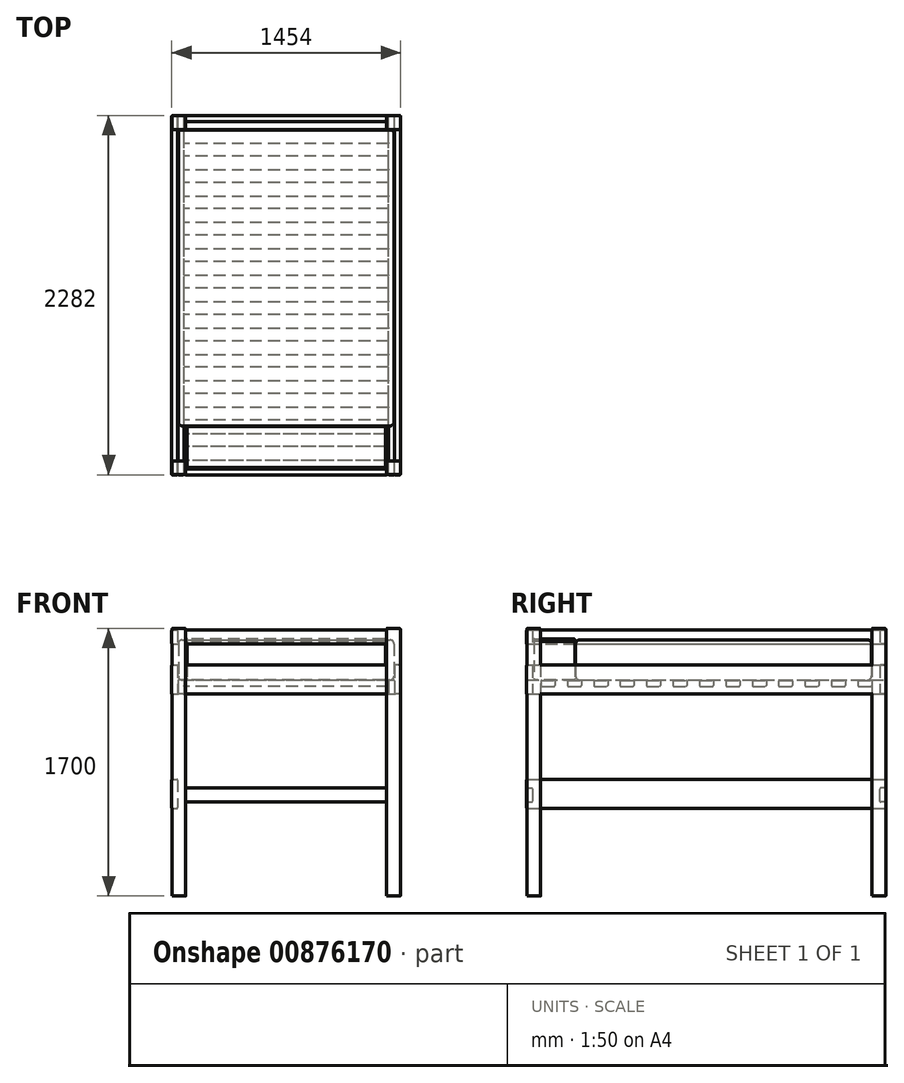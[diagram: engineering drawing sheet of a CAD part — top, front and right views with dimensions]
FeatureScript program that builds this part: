
annotation { "Feature Type Name" : "Feature", "Feature Type Description" : "" }
export const myFeature = defineFeature(function(context is Context, id is Id, definition is map)
    precondition{}
    {
        {
            var Q0;
            Q0=qCreatedBy(makeId("Top.planeOp"),FACE);
            var sketch = newSketch(context, id + "F0", { "sketchPlane" : qUnion([Q0])});
            skLineSegment(sketch, "E0.bottom", {"start": v(-720, -1052.5) * mm, "end": v(-642.5, -1052.5) * mm});
            skLineSegment(sketch, "E0.top", {"start": v(-720, -1140) * mm, "end": v(-642.5, -1140) * mm});
            skLineSegment(sketch, "E0.left", {"start": v(-725, -1057.5) * mm, "end": v(-725, -1135) * mm});
            skLineSegment(sketch, "E0.right", {"start": v(-637.5, -1057.5) * mm, "end": v(-637.5, -1135) * mm});
            skLineSegment(sketch, "E1.bottom", {"start": v(-720, 1140) * mm, "end": v(-642.5, 1140) * mm});
            skLineSegment(sketch, "E1.top", {"start": v(-720, 1052.5) * mm, "end": v(-642.5, 1052.5) * mm});
            skLineSegment(sketch, "E1.left", {"start": v(-725, 1135) * mm, "end": v(-725, 1057.5) * mm});
            skLineSegment(sketch, "E1.right", {"start": v(-637.5, 1135) * mm, "end": v(-637.5, 1057.5) * mm});
            skLineSegment(sketch, "E2.bottom", {"start": v(642.5, 1140) * mm, "end": v(720, 1140) * mm});
            skLineSegment(sketch, "E2.top", {"start": v(642.5, 1052.5) * mm, "end": v(720, 1052.5) * mm});
            skLineSegment(sketch, "E2.left", {"start": v(637.5, 1135) * mm, "end": v(637.5, 1057.5) * mm});
            skLineSegment(sketch, "E2.right", {"start": v(725, 1135) * mm, "end": v(725, 1057.5) * mm});
            skLineSegment(sketch, "E3.bottom", {"start": v(642.5, -1052.5) * mm, "end": v(720, -1052.5) * mm});
            skLineSegment(sketch, "E3.top", {"start": v(642.5, -1140) * mm, "end": v(720, -1140) * mm});
            skLineSegment(sketch, "E3.left", {"start": v(637.5, -1057.5) * mm, "end": v(637.5, -1135) * mm});
            skLineSegment(sketch, "E3.right", {"start": v(725, -1057.5) * mm, "end": v(725, -1135) * mm});
            skPoint(sketch, "E4.visualSharp", {"position": v(-637.5, 1052.5) * mm});
            skArc(sketch, "E4.filletArc", {"start": v(-642.5, 1052.5) * mm, "mid": v(-638.96, 1053.96) * mm, "end": v(-637.5, 1057.5) * mm});
            skPoint(sketch, "E5.visualSharp", {"position": v(-725, 1140) * mm});
            skArc(sketch, "E5.filletArc", {"start": v(-720, 1140) * mm, "mid": v(-723.54, 1138.54) * mm, "end": v(-725, 1135) * mm});
            skPoint(sketch, "E6.visualSharp", {"position": v(-725, 1052.5) * mm});
            skArc(sketch, "E6.filletArc", {"start": v(-725, 1057.5) * mm, "mid": v(-723.54, 1053.96) * mm, "end": v(-720, 1052.5) * mm});
            skPoint(sketch, "E7.visualSharp", {"position": v(-637.5, 1140) * mm});
            skArc(sketch, "E7.filletArc", {"start": v(-637.5, 1135) * mm, "mid": v(-638.96, 1138.54) * mm, "end": v(-642.5, 1140) * mm});
            skPoint(sketch, "E8.visualSharp", {"position": v(637.5, 1052.5) * mm});
            skArc(sketch, "E8.filletArc", {"start": v(637.5, 1057.5) * mm, "mid": v(638.96, 1053.96) * mm, "end": v(642.5, 1052.5) * mm});
            skPoint(sketch, "E9.visualSharp", {"position": v(725, 1140) * mm});
            skArc(sketch, "E9.filletArc", {"start": v(725, 1135) * mm, "mid": v(723.54, 1138.54) * mm, "end": v(720, 1140) * mm});
            skPoint(sketch, "E10.visualSharp", {"position": v(725, 1052.5) * mm});
            skArc(sketch, "E10.filletArc", {"start": v(720, 1052.5) * mm, "mid": v(723.54, 1053.96) * mm, "end": v(725, 1057.5) * mm});
            skPoint(sketch, "E11.visualSharp", {"position": v(637.5, 1140) * mm});
            skArc(sketch, "E11.filletArc", {"start": v(642.5, 1140) * mm, "mid": v(638.96, 1138.54) * mm, "end": v(637.5, 1135) * mm});
            skPoint(sketch, "E12.visualSharp", {"position": v(-637.5, -1140) * mm});
            skArc(sketch, "E12.filletArc", {"start": v(-642.5, -1140) * mm, "mid": v(-638.96, -1138.54) * mm, "end": v(-637.5, -1135) * mm});
            skPoint(sketch, "E13.visualSharp", {"position": v(-725, -1052.5) * mm});
            skArc(sketch, "E13.filletArc", {"start": v(-720, -1052.5) * mm, "mid": v(-723.54, -1053.96) * mm, "end": v(-725, -1057.5) * mm});
            skPoint(sketch, "E14.visualSharp", {"position": v(-725, -1140) * mm});
            skArc(sketch, "E14.filletArc", {"start": v(-725, -1135) * mm, "mid": v(-723.54, -1138.54) * mm, "end": v(-720, -1140) * mm});
            skPoint(sketch, "E15.visualSharp", {"position": v(-637.5, -1052.5) * mm});
            skArc(sketch, "E15.filletArc", {"start": v(-637.5, -1057.5) * mm, "mid": v(-638.96, -1053.96) * mm, "end": v(-642.5, -1052.5) * mm});
            skPoint(sketch, "E16.visualSharp", {"position": v(725, -1140) * mm});
            skArc(sketch, "E16.filletArc", {"start": v(720, -1140) * mm, "mid": v(723.54, -1138.54) * mm, "end": v(725, -1135) * mm});
            skPoint(sketch, "E17.visualSharp", {"position": v(637.5, -1052.5) * mm});
            skArc(sketch, "E17.filletArc", {"start": v(642.5, -1052.5) * mm, "mid": v(638.96, -1053.96) * mm, "end": v(637.5, -1057.5) * mm});
            skPoint(sketch, "E18.visualSharp", {"position": v(637.5, -1140) * mm});
            skArc(sketch, "E18.filletArc", {"start": v(637.5, -1135) * mm, "mid": v(638.96, -1138.54) * mm, "end": v(642.5, -1140) * mm});
            skPoint(sketch, "E19.visualSharp", {"position": v(725, -1052.5) * mm});
            skArc(sketch, "E19.filletArc", {"start": v(725, -1057.5) * mm, "mid": v(723.54, -1053.96) * mm, "end": v(720, -1052.5) * mm});
            skSolve(sketch);
        }
        {
            var Q0;
            Q0 = qSketchRegion(id + "F0", true);
            extrude(context, id + "F1", {"entities" : qUnion([Q0]), "depth" : 1700 * mm, "offsetDistance" : 25 * mm});
        }
        {
            var Q0;
            Q0=qCreatedBy(makeId("Front.planeOp"),FACE);
            var sketch = newSketch(context, id + "F2", { "sketchPlane" : qUnion([Q0])});
            skLineSegment(sketch, "E20.bottom", {"start": v(-722, 1466) * mm, "end": v(-694, 1466) * mm});
            skLineSegment(sketch, "E20.top", {"start": v(-722, 1282) * mm, "end": v(-694, 1282) * mm});
            skLineSegment(sketch, "E20.left", {"start": v(-727, 1461) * mm, "end": v(-727, 1287) * mm});
            skLineSegment(sketch, "E20.right", {"start": v(-689, 1461) * mm, "end": v(-689, 1287) * mm});
            skLineSegment(sketch, "E21.bottom", {"start": v(722, 1466) * mm, "end": v(694, 1466) * mm});
            skLineSegment(sketch, "E21.top", {"start": v(722, 1282) * mm, "end": v(694, 1282) * mm});
            skLineSegment(sketch, "E21.left", {"start": v(727, 1461) * mm, "end": v(727, 1287) * mm});
            skLineSegment(sketch, "E21.right", {"start": v(689, 1461) * mm, "end": v(689, 1287) * mm});
            skLineSegment(sketch, "E22.bottom", {"start": v(-722, 740) * mm, "end": v(-694, 740) * mm});
            skLineSegment(sketch, "E22.top", {"start": v(-722, 556) * mm, "end": v(-694, 556) * mm});
            skLineSegment(sketch, "E22.left", {"start": v(-727, 735) * mm, "end": v(-727, 561) * mm});
            skLineSegment(sketch, "E22.right", {"start": v(-689, 735) * mm, "end": v(-689, 561) * mm});
            skLineSegment(sketch, "E23.bottom", {"start": v(-655, 1371) * mm, "end": v(-683, 1371) * mm});
            skLineSegment(sketch, "E23.top", {"start": v(-655, 1282) * mm, "end": v(-683, 1282) * mm});
            skLineSegment(sketch, "E23.left", {"start": v(-650, 1366) * mm, "end": v(-650, 1287) * mm});
            skLineSegment(sketch, "E23.right", {"start": v(-688, 1366) * mm, "end": v(-688, 1287) * mm});
            skLineSegment(sketch, "E24.bottom", {"start": v(655, 1371) * mm, "end": v(683, 1371) * mm});
            skLineSegment(sketch, "E24.top", {"start": v(655, 1282) * mm, "end": v(683, 1282) * mm});
            skLineSegment(sketch, "E24.left", {"start": v(650, 1366) * mm, "end": v(650, 1287) * mm});
            skLineSegment(sketch, "E24.right", {"start": v(688, 1366) * mm, "end": v(688, 1287) * mm});
            skPoint(sketch, "E25.visualSharp", {"position": v(-688, 1282) * mm});
            skArc(sketch, "E25.filletArc", {"start": v(-688, 1287) * mm, "mid": v(-686.54, 1283.46) * mm, "end": v(-683, 1282) * mm});
            skPoint(sketch, "E26.visualSharp", {"position": v(-688, 1371) * mm});
            skArc(sketch, "E26.filletArc", {"start": v(-683, 1371) * mm, "mid": v(-686.54, 1369.54) * mm, "end": v(-688, 1366) * mm});
            skPoint(sketch, "E27.visualSharp", {"position": v(-650, 1371) * mm});
            skArc(sketch, "E27.filletArc", {"start": v(-650, 1366) * mm, "mid": v(-651.46, 1369.54) * mm, "end": v(-655, 1371) * mm});
            skPoint(sketch, "E28.visualSharp", {"position": v(-650, 1282) * mm});
            skArc(sketch, "E28.filletArc", {"start": v(-655, 1282) * mm, "mid": v(-651.46, 1283.46) * mm, "end": v(-650, 1287) * mm});
            skPoint(sketch, "E29.visualSharp", {"position": v(-689, 1282) * mm});
            skArc(sketch, "E29.filletArc", {"start": v(-694, 1282) * mm, "mid": v(-690.46, 1283.46) * mm, "end": v(-689, 1287) * mm});
            skPoint(sketch, "E30.visualSharp", {"position": v(-727, 1282) * mm});
            skArc(sketch, "E30.filletArc", {"start": v(-727, 1287) * mm, "mid": v(-725.54, 1283.46) * mm, "end": v(-722, 1282) * mm});
            skPoint(sketch, "E31.visualSharp", {"position": v(-727, 1466) * mm});
            skArc(sketch, "E31.filletArc", {"start": v(-722, 1466) * mm, "mid": v(-725.54, 1464.54) * mm, "end": v(-727, 1461) * mm});
            skPoint(sketch, "E32.visualSharp", {"position": v(-689, 1466) * mm});
            skArc(sketch, "E32.filletArc", {"start": v(-689, 1461) * mm, "mid": v(-690.46, 1464.54) * mm, "end": v(-694, 1466) * mm});
            skPoint(sketch, "E33.visualSharp", {"position": v(650, 1371) * mm});
            skArc(sketch, "E33.filletArc", {"start": v(655, 1371) * mm, "mid": v(651.46, 1369.54) * mm, "end": v(650, 1366) * mm});
            skPoint(sketch, "E34.visualSharp", {"position": v(688, 1371) * mm});
            skArc(sketch, "E34.filletArc", {"start": v(688, 1366) * mm, "mid": v(686.54, 1369.54) * mm, "end": v(683, 1371) * mm});
            skPoint(sketch, "E35.visualSharp", {"position": v(688, 1282) * mm});
            skArc(sketch, "E35.filletArc", {"start": v(683, 1282) * mm, "mid": v(686.54, 1283.46) * mm, "end": v(688, 1287) * mm});
            skPoint(sketch, "E36.visualSharp", {"position": v(650, 1282) * mm});
            skArc(sketch, "E36.filletArc", {"start": v(650, 1287) * mm, "mid": v(651.46, 1283.46) * mm, "end": v(655, 1282) * mm});
            skPoint(sketch, "E37.visualSharp", {"position": v(689, 1282) * mm});
            skArc(sketch, "E37.filletArc", {"start": v(689, 1287) * mm, "mid": v(690.46, 1283.46) * mm, "end": v(694, 1282) * mm});
            skPoint(sketch, "E38.visualSharp", {"position": v(727, 1282) * mm});
            skArc(sketch, "E38.filletArc", {"start": v(722, 1282) * mm, "mid": v(725.54, 1283.46) * mm, "end": v(727, 1287) * mm});
            skArc(sketch, "E39.filletArc", {"start": v(694, 1466) * mm, "mid": v(690.46, 1464.54) * mm, "end": v(689, 1461) * mm});
            skArc(sketch, "E40.filletArc", {"start": v(727, 1461) * mm, "mid": v(725.54, 1464.54) * mm, "end": v(722, 1466) * mm});
            skPoint(sketch, "E41.visualSharp", {"position": v(-727, 740) * mm});
            skArc(sketch, "E41.filletArc", {"start": v(-722, 740) * mm, "mid": v(-725.54, 738.54) * mm, "end": v(-727, 735) * mm});
            skPoint(sketch, "E42.visualSharp", {"position": v(-727, 556) * mm});
            skArc(sketch, "E42.filletArc", {"start": v(-727, 561) * mm, "mid": v(-725.54, 557.46) * mm, "end": v(-722, 556) * mm});
            skPoint(sketch, "E43.visualSharp", {"position": v(-689, 740) * mm});
            skArc(sketch, "E43.filletArc", {"start": v(-689, 735) * mm, "mid": v(-690.46, 738.54) * mm, "end": v(-694, 740) * mm});
            skPoint(sketch, "E44.visualSharp", {"position": v(-689, 556) * mm});
            skArc(sketch, "E44.filletArc", {"start": v(-694, 556) * mm, "mid": v(-690.46, 557.46) * mm, "end": v(-689, 561) * mm});
            skLineSegment(sketch, "E45.bottom", {"start": v(-722, 1689) * mm, "end": v(-694, 1689) * mm});
            skLineSegment(sketch, "E45.top", {"start": v(-722, 1600) * mm, "end": v(-694, 1600) * mm});
            skLineSegment(sketch, "E45.left", {"start": v(-727, 1684) * mm, "end": v(-727, 1605) * mm});
            skLineSegment(sketch, "E45.right", {"start": v(-689, 1684) * mm, "end": v(-689, 1605) * mm});
            skPoint(sketch, "E46.visualSharp", {"position": v(-727, 1600) * mm});
            skArc(sketch, "E46.filletArc", {"start": v(-727, 1605) * mm, "mid": v(-725.54, 1601.46) * mm, "end": v(-722, 1600) * mm});
            skPoint(sketch, "E47.visualSharp", {"position": v(-689, 1600) * mm});
            skArc(sketch, "E47.filletArc", {"start": v(-694, 1600) * mm, "mid": v(-690.46, 1601.46) * mm, "end": v(-689, 1605) * mm});
            skPoint(sketch, "E48.visualSharp", {"position": v(-727, 1689) * mm});
            skArc(sketch, "E48.filletArc", {"start": v(-722, 1689) * mm, "mid": v(-725.54, 1687.54) * mm, "end": v(-727, 1684) * mm});
            skPoint(sketch, "E49.visualSharp", {"position": v(-689, 1689) * mm});
            skArc(sketch, "E49.filletArc", {"start": v(-689, 1684) * mm, "mid": v(-690.46, 1687.54) * mm, "end": v(-694, 1689) * mm});
            skSolve(sketch);
        }
        {
            var Q0;
            Q0 = qSketchRegion(id + "F2", true);
            extrude(context, id + "F3", {"entities" : qUnion([Q0]), "depth" : 1141 * mm, "offsetDistance" : 25 * mm, "hasSecondDirection" : true, "secondDirectionOppositeDirection" : true, "secondDirectionDepth" : 1141 * mm});
        }
        {
            var Q0;
            Q0=qCreatedBy(makeId("Right.planeOp"),FACE);
            var sketch = newSketch(context, id + "F4", { "sketchPlane" : qUnion([Q0])});
            skLineSegment(sketch, "E50.bottom", {"start": v(-1136, 1689) * mm, "end": v(-1108, 1689) * mm});
            skLineSegment(sketch, "E50.top", {"start": v(-1136, 1600) * mm, "end": v(-1108, 1600) * mm});
            skLineSegment(sketch, "E50.left", {"start": v(-1141, 1684) * mm, "end": v(-1141, 1605) * mm});
            skLineSegment(sketch, "E50.right", {"start": v(-1103, 1684) * mm, "end": v(-1103, 1605) * mm});
            skLineSegment(sketch, "E51.bottom", {"start": v(1136, 1689) * mm, "end": v(1108, 1689) * mm});
            skLineSegment(sketch, "E51.top", {"start": v(1136, 1600) * mm, "end": v(1108, 1600) * mm});
            skLineSegment(sketch, "E51.left", {"start": v(1141, 1684) * mm, "end": v(1141, 1605) * mm});
            skLineSegment(sketch, "E51.right", {"start": v(1103, 1684) * mm, "end": v(1103, 1605) * mm});
            skLineSegment(sketch, "E52.bottom", {"start": v(-1136, 1466) * mm, "end": v(-1108, 1466) * mm});
            skLineSegment(sketch, "E52.top", {"start": v(-1135.9, 1282) * mm, "end": v(-1108, 1282) * mm});
            skLineSegment(sketch, "E52.left", {"start": v(-1141, 1461) * mm, "end": v(-1141, 1287.1) * mm});
            skLineSegment(sketch, "E52.right", {"start": v(-1103, 1461) * mm, "end": v(-1103, 1287) * mm});
            skLineSegment(sketch, "E53.bottom", {"start": v(1136, 1466) * mm, "end": v(1108, 1466) * mm});
            skLineSegment(sketch, "E53.top", {"start": v(1136, 1282) * mm, "end": v(1108, 1282) * mm});
            skLineSegment(sketch, "E53.left", {"start": v(1141, 1461) * mm, "end": v(1141, 1287) * mm});
            skLineSegment(sketch, "E53.right", {"start": v(1103, 1461) * mm, "end": v(1103, 1287) * mm});
            skLineSegment(sketch, "E54.bottom", {"start": v(-1136, 685) * mm, "end": v(-1108, 685) * mm});
            skLineSegment(sketch, "E54.top", {"start": v(-1136, 596) * mm, "end": v(-1108, 596) * mm});
            skLineSegment(sketch, "E54.left", {"start": v(-1141, 680) * mm, "end": v(-1141, 601) * mm});
            skLineSegment(sketch, "E54.right", {"start": v(-1103, 680) * mm, "end": v(-1103, 601) * mm});
            skLineSegment(sketch, "E55.bottom", {"start": v(1136, 596) * mm, "end": v(1108, 596) * mm});
            skLineSegment(sketch, "E55.top", {"start": v(1136, 685) * mm, "end": v(1108, 685) * mm});
            skLineSegment(sketch, "E55.left", {"start": v(1141, 601) * mm, "end": v(1141, 680) * mm});
            skLineSegment(sketch, "E55.right", {"start": v(1103, 601) * mm, "end": v(1103, 680) * mm});
            skPoint(sketch, "E56.visualSharp", {"position": v(-1141, 1689) * mm});
            skArc(sketch, "E56.filletArc", {"start": v(-1136, 1689) * mm, "mid": v(-1139.54, 1687.54) * mm, "end": v(-1141, 1684) * mm});
            skPoint(sketch, "E57.visualSharp", {"position": v(-1103, 1600) * mm});
            skArc(sketch, "E57.filletArc", {"start": v(-1108, 1600) * mm, "mid": v(-1104.46, 1601.46) * mm, "end": v(-1103, 1605) * mm});
            skPoint(sketch, "E58.visualSharp", {"position": v(-1103, 1689) * mm});
            skArc(sketch, "E58.filletArc", {"start": v(-1103, 1684) * mm, "mid": v(-1104.46, 1687.54) * mm, "end": v(-1108, 1689) * mm});
            skPoint(sketch, "E59.visualSharp", {"position": v(-1141, 1600) * mm});
            skArc(sketch, "E59.filletArc", {"start": v(-1141, 1605) * mm, "mid": v(-1139.54, 1601.46) * mm, "end": v(-1136, 1600) * mm});
            skPoint(sketch, "E60.visualSharp", {"position": v(-1141, 1466) * mm});
            skArc(sketch, "E60.filletArc", {"start": v(-1136, 1466) * mm, "mid": v(-1139.54, 1464.54) * mm, "end": v(-1141, 1461) * mm});
            skPoint(sketch, "E61.visualSharp", {"position": v(-1103, 1282) * mm});
            skArc(sketch, "E61.filletArc", {"start": v(-1108, 1282) * mm, "mid": v(-1104.46, 1283.46) * mm, "end": v(-1103, 1287) * mm});
            skPoint(sketch, "E62.visualSharp", {"position": v(-1103, 1466) * mm});
            skArc(sketch, "E62.filletArc", {"start": v(-1103, 1461) * mm, "mid": v(-1104.46, 1464.54) * mm, "end": v(-1108, 1466) * mm});
            skPoint(sketch, "E63.visualSharp", {"position": v(-1141, 1282) * mm});
            skArc(sketch, "E63.filletArc", {"start": v(-1141, 1287.1) * mm, "mid": v(-1139.5, 1283.5) * mm, "end": v(-1135.9, 1282) * mm});
            skPoint(sketch, "E64.visualSharp", {"position": v(-1141, 685) * mm});
            skArc(sketch, "E64.filletArc", {"start": v(-1136, 685) * mm, "mid": v(-1139.54, 683.54) * mm, "end": v(-1141, 680) * mm});
            skPoint(sketch, "E65.visualSharp", {"position": v(-1103, 596) * mm});
            skArc(sketch, "E65.filletArc", {"start": v(-1108, 596) * mm, "mid": v(-1104.46, 597.46) * mm, "end": v(-1103, 601) * mm});
            skPoint(sketch, "E66.visualSharp", {"position": v(-1103, 685) * mm});
            skArc(sketch, "E66.filletArc", {"start": v(-1103, 680) * mm, "mid": v(-1104.46, 683.54) * mm, "end": v(-1108, 685) * mm});
            skPoint(sketch, "E67.visualSharp", {"position": v(-1141, 596) * mm});
            skArc(sketch, "E67.filletArc", {"start": v(-1141, 601) * mm, "mid": v(-1139.54, 597.46) * mm, "end": v(-1136, 596) * mm});
            skPoint(sketch, "E68.visualSharp", {"position": v(1103, 685) * mm});
            skArc(sketch, "E68.filletArc", {"start": v(1108, 685) * mm, "mid": v(1104.46, 683.54) * mm, "end": v(1103, 680) * mm});
            skPoint(sketch, "E69.visualSharp", {"position": v(1141, 596) * mm});
            skArc(sketch, "E69.filletArc", {"start": v(1136, 596) * mm, "mid": v(1139.54, 597.46) * mm, "end": v(1141, 601) * mm});
            skPoint(sketch, "E70.visualSharp", {"position": v(1141, 685) * mm});
            skArc(sketch, "E70.filletArc", {"start": v(1141, 680) * mm, "mid": v(1139.54, 683.54) * mm, "end": v(1136, 685) * mm});
            skPoint(sketch, "E71.visualSharp", {"position": v(1103, 596) * mm});
            skArc(sketch, "E71.filletArc", {"start": v(1103, 601) * mm, "mid": v(1104.46, 597.46) * mm, "end": v(1108, 596) * mm});
            skPoint(sketch, "E72.visualSharp", {"position": v(1103, 1466) * mm});
            skArc(sketch, "E72.filletArc", {"start": v(1108, 1466) * mm, "mid": v(1104.46, 1464.54) * mm, "end": v(1103, 1461) * mm});
            skPoint(sketch, "E73.visualSharp", {"position": v(1141, 1282) * mm});
            skArc(sketch, "E73.filletArc", {"start": v(1136, 1282) * mm, "mid": v(1139.54, 1283.46) * mm, "end": v(1141, 1287) * mm});
            skPoint(sketch, "E74.visualSharp", {"position": v(1141, 1466) * mm});
            skArc(sketch, "E74.filletArc", {"start": v(1141, 1461) * mm, "mid": v(1139.54, 1464.54) * mm, "end": v(1136, 1466) * mm});
            skPoint(sketch, "E75.visualSharp", {"position": v(1103, 1282) * mm});
            skArc(sketch, "E75.filletArc", {"start": v(1103, 1287) * mm, "mid": v(1104.46, 1283.46) * mm, "end": v(1108, 1282) * mm});
            skPoint(sketch, "E76.visualSharp", {"position": v(1103, 1689) * mm});
            skArc(sketch, "E76.filletArc", {"start": v(1108, 1689) * mm, "mid": v(1104.46, 1687.54) * mm, "end": v(1103, 1684) * mm});
            skPoint(sketch, "E77.visualSharp", {"position": v(1141, 1600) * mm});
            skArc(sketch, "E77.filletArc", {"start": v(1136, 1600) * mm, "mid": v(1139.54, 1601.46) * mm, "end": v(1141, 1605) * mm});
            skPoint(sketch, "E78.visualSharp", {"position": v(1141, 1689) * mm});
            skArc(sketch, "E78.filletArc", {"start": v(1141, 1684) * mm, "mid": v(1139.54, 1687.54) * mm, "end": v(1136, 1689) * mm});
            skPoint(sketch, "E79.visualSharp", {"position": v(1103, 1600) * mm});
            skArc(sketch, "E79.filletArc", {"start": v(1103, 1605) * mm, "mid": v(1104.46, 1601.46) * mm, "end": v(1108, 1600) * mm});
            skSolve(sketch);
        }
        {
            var Q0;
            Q0 = qSketchRegion(id + "F4", true);
            extrude(context, id + "F5", {"entities" : qUnion([Q0]), "depth" : 637.5 * mm, "offsetDistance" : 25 * mm, "hasSecondDirection" : true, "secondDirectionOppositeDirection" : true, "secondDirectionDepth" : 637.5 * mm});
        }
        {
            var Q0;
            Q0=qCreatedBy(makeId("Front.planeOp"),FACE);
            var sketch = newSketch(context, id + "F6", { "sketchPlane" : qUnion([Q0])});
            skLineSegment(sketch, "E80.bottom", {"start": v(-660, 1626) * mm, "end": v(660, 1626) * mm});
            skLineSegment(sketch, "E80.top", {"start": v(-660, 1372) * mm, "end": v(660, 1372) * mm});
            skLineSegment(sketch, "E80.left", {"start": v(-685, 1601) * mm, "end": v(-685, 1397) * mm});
            skLineSegment(sketch, "E80.right", {"start": v(685, 1601) * mm, "end": v(685, 1397) * mm});
            skPoint(sketch, "E81.visualSharp", {"position": v(-685, 1626) * mm});
            skArc(sketch, "E81.filletArc", {"start": v(-660, 1626) * mm, "mid": v(-677.68, 1618.68) * mm, "end": v(-685, 1601) * mm});
            skPoint(sketch, "E82.visualSharp", {"position": v(-685, 1372) * mm});
            skArc(sketch, "E82.filletArc", {"start": v(-685, 1397) * mm, "mid": v(-677.68, 1379.32) * mm, "end": v(-660, 1372) * mm});
            skPoint(sketch, "E83.visualSharp", {"position": v(685, 1626) * mm});
            skArc(sketch, "E83.filletArc", {"start": v(685, 1601) * mm, "mid": v(677.68, 1618.68) * mm, "end": v(660, 1626) * mm});
            skPoint(sketch, "E84.visualSharp", {"position": v(685, 1372) * mm});
            skArc(sketch, "E84.filletArc", {"start": v(660, 1372) * mm, "mid": v(677.68, 1379.32) * mm, "end": v(685, 1397) * mm});
            skSolve(sketch);
        }
        {
            var Q0;
            Q0 = qSketchRegion(id + "F6", true);
            extrude(context, id + "F7", {"entities" : qUnion([Q0]), "depth" : 830 * mm, "offsetDistance" : 25 * mm, "hasSecondDirection" : true, "secondDirectionOppositeDirection" : true, "secondDirectionDepth" : 1050 * mm});
        }
        {
            var Q0;
            Q0=qCreatedBy(makeId("Right.planeOp"),FACE);
            var sketch = newSketch(context, id + "F8", { "sketchPlane" : qUnion([Q0])});
            skLineSegment(sketch, "E85.bottom", {"start": v(-835, 1617) * mm, "end": v(-1095, 1617) * mm});
            skLineSegment(sketch, "E85.top", {"start": v(-835, 1372) * mm, "end": v(-1095, 1372) * mm});
            skLineSegment(sketch, "E85.left", {"start": v(-835, 1617) * mm, "end": v(-835, 1372) * mm});
            skLineSegment(sketch, "E85.right", {"start": v(-1095, 1617) * mm, "end": v(-1095, 1372) * mm});
            skLineSegment(sketch, "E86.bottom", {"start": v(-1095, 1632) * mm, "end": v(-835, 1632) * mm});
            skLineSegment(sketch, "E86.top", {"start": v(-1095, 1619.5) * mm, "end": v(-835, 1619.5) * mm});
            skLineSegment(sketch, "E86.left", {"start": v(-1095, 1632) * mm, "end": v(-1095, 1619.5) * mm});
            skLineSegment(sketch, "E86.right", {"start": v(-835, 1632) * mm, "end": v(-835, 1619.5) * mm});
            skSolve(sketch);
        }
        {
            var Q0;
            Q0 = qSketchRegion(id + "F8", true);
            extrude(context, id + "F9", {"entities" : qUnion([Q0]), "depth" : 630 * mm, "offsetDistance" : 25 * mm, "hasSecondDirection" : true, "secondDirectionOppositeDirection" : true, "secondDirectionDepth" : 630 * mm});
        }
        {
            var Q0;
            Q0=qCreatedBy(makeId("Right.planeOp"),FACE);
            var sketch = newSketch(context, id + "F10", { "sketchPlane" : qUnion([Q0])});
            skLineSegment(sketch, "E87.bottom", {"start": v(-1045, 1370) * mm, "end": v(-966, 1370) * mm});
            skLineSegment(sketch, "E87.top", {"start": v(-1045, 1332) * mm, "end": v(-966, 1332) * mm});
            skLineSegment(sketch, "E87.left", {"start": v(-1050, 1365) * mm, "end": v(-1050, 1337) * mm});
            skLineSegment(sketch, "E87.right", {"start": v(-961, 1365) * mm, "end": v(-961, 1337) * mm});
            skPoint(sketch, "E88.visualSharp", {"position": v(-961, 1370) * mm});
            skArc(sketch, "E88.filletArc", {"start": v(-961, 1365) * mm, "mid": v(-962.46, 1368.54) * mm, "end": v(-966, 1370) * mm});
            skPoint(sketch, "E89.visualSharp", {"position": v(-1050, 1332) * mm});
            skArc(sketch, "E89.filletArc", {"start": v(-1050, 1337) * mm, "mid": v(-1048.54, 1333.46) * mm, "end": v(-1045, 1332) * mm});
            skPoint(sketch, "E90.visualSharp", {"position": v(-1050, 1370) * mm});
            skArc(sketch, "E90.filletArc", {"start": v(-1045, 1370) * mm, "mid": v(-1048.54, 1368.54) * mm, "end": v(-1050, 1365) * mm});
            skPoint(sketch, "E91.visualSharp", {"position": v(-961, 1332) * mm});
            skArc(sketch, "E91.filletArc", {"start": v(-966, 1332) * mm, "mid": v(-962.46, 1333.46) * mm, "end": v(-961, 1337) * mm});
            skPoint(sketch, "E92.1.0.0", {"position": v(-793.25, 1370) * mm});
            skLineSegment(sketch, "E92.1.0.1", {"start": v(-877.25, 1370) * mm, "end": v(-798.25, 1370) * mm});
            skLineSegment(sketch, "E92.1.0.2", {"start": v(-877.25, 1332) * mm, "end": v(-798.25, 1332) * mm});
            skLineSegment(sketch, "E92.1.0.3", {"start": v(-793.25, 1365) * mm, "end": v(-793.25, 1337) * mm});
            skLineSegment(sketch, "E92.1.0.4", {"start": v(-882.25, 1365) * mm, "end": v(-882.25, 1337) * mm});
            skPoint(sketch, "E92.1.0.5", {"position": v(-882.25, 1370) * mm});
            skPoint(sketch, "E92.1.0.6", {"position": v(-793.25, 1332) * mm});
            skPoint(sketch, "E92.1.0.7", {"position": v(-882.25, 1332) * mm});
            skArc(sketch, "E92.1.0.8", {"start": v(-798.25, 1332) * mm, "mid": v(-794.71, 1333.46) * mm, "end": v(-793.25, 1337) * mm});
            skArc(sketch, "E92.1.0.9", {"start": v(-793.25, 1365) * mm, "mid": v(-794.71, 1368.54) * mm, "end": v(-798.25, 1370) * mm});
            skArc(sketch, "E92.1.0.10", {"start": v(-882.25, 1337) * mm, "mid": v(-880.79, 1333.46) * mm, "end": v(-877.25, 1332) * mm});
            skArc(sketch, "E92.1.0.11", {"start": v(-877.25, 1370) * mm, "mid": v(-880.79, 1368.54) * mm, "end": v(-882.25, 1365) * mm});
            skPoint(sketch, "E92.2.0.0", {"position": v(-625.5, 1370) * mm});
            skLineSegment(sketch, "E92.2.0.1", {"start": v(-709.5, 1370) * mm, "end": v(-630.5, 1370) * mm});
            skLineSegment(sketch, "E92.2.0.2", {"start": v(-709.5, 1332) * mm, "end": v(-630.5, 1332) * mm});
            skLineSegment(sketch, "E92.2.0.3", {"start": v(-625.5, 1365) * mm, "end": v(-625.5, 1337) * mm});
            skLineSegment(sketch, "E92.2.0.4", {"start": v(-714.5, 1365) * mm, "end": v(-714.5, 1337) * mm});
            skPoint(sketch, "E92.2.0.5", {"position": v(-714.5, 1370) * mm});
            skPoint(sketch, "E92.2.0.6", {"position": v(-625.5, 1332) * mm});
            skPoint(sketch, "E92.2.0.7", {"position": v(-714.5, 1332) * mm});
            skArc(sketch, "E92.2.0.8", {"start": v(-630.5, 1332) * mm, "mid": v(-626.96, 1333.46) * mm, "end": v(-625.5, 1337) * mm});
            skArc(sketch, "E92.2.0.9", {"start": v(-625.5, 1365) * mm, "mid": v(-626.96, 1368.54) * mm, "end": v(-630.5, 1370) * mm});
            skArc(sketch, "E92.2.0.10", {"start": v(-714.5, 1337) * mm, "mid": v(-713.04, 1333.46) * mm, "end": v(-709.5, 1332) * mm});
            skArc(sketch, "E92.2.0.11", {"start": v(-709.5, 1370) * mm, "mid": v(-713.04, 1368.54) * mm, "end": v(-714.5, 1365) * mm});
            skPoint(sketch, "E92.3.0.0", {"position": v(-457.75, 1370) * mm});
            skLineSegment(sketch, "E92.3.0.1", {"start": v(-541.75, 1370) * mm, "end": v(-462.75, 1370) * mm});
            skLineSegment(sketch, "E92.3.0.2", {"start": v(-541.75, 1332) * mm, "end": v(-462.75, 1332) * mm});
            skLineSegment(sketch, "E92.3.0.3", {"start": v(-457.75, 1365) * mm, "end": v(-457.75, 1337) * mm});
            skLineSegment(sketch, "E92.3.0.4", {"start": v(-546.75, 1365) * mm, "end": v(-546.75, 1337) * mm});
            skPoint(sketch, "E92.3.0.5", {"position": v(-546.75, 1370) * mm});
            skPoint(sketch, "E92.3.0.6", {"position": v(-457.75, 1332) * mm});
            skPoint(sketch, "E92.3.0.7", {"position": v(-546.75, 1332) * mm});
            skArc(sketch, "E92.3.0.8", {"start": v(-462.75, 1332) * mm, "mid": v(-459.21, 1333.46) * mm, "end": v(-457.75, 1337) * mm});
            skArc(sketch, "E92.3.0.9", {"start": v(-457.75, 1365) * mm, "mid": v(-459.21, 1368.54) * mm, "end": v(-462.75, 1370) * mm});
            skArc(sketch, "E92.3.0.10", {"start": v(-546.75, 1337) * mm, "mid": v(-545.29, 1333.46) * mm, "end": v(-541.75, 1332) * mm});
            skArc(sketch, "E92.3.0.11", {"start": v(-541.75, 1370) * mm, "mid": v(-545.29, 1368.54) * mm, "end": v(-546.75, 1365) * mm});
            skPoint(sketch, "E92.4.0.0", {"position": v(-290, 1370) * mm});
            skLineSegment(sketch, "E92.4.0.1", {"start": v(-374, 1370) * mm, "end": v(-295, 1370) * mm});
            skLineSegment(sketch, "E92.4.0.2", {"start": v(-374, 1332) * mm, "end": v(-295, 1332) * mm});
            skLineSegment(sketch, "E92.4.0.3", {"start": v(-290, 1365) * mm, "end": v(-290, 1337) * mm});
            skLineSegment(sketch, "E92.4.0.4", {"start": v(-379, 1365) * mm, "end": v(-379, 1337) * mm});
            skPoint(sketch, "E92.4.0.5", {"position": v(-379, 1370) * mm});
            skPoint(sketch, "E92.4.0.6", {"position": v(-290, 1332) * mm});
            skPoint(sketch, "E92.4.0.7", {"position": v(-379, 1332) * mm});
            skArc(sketch, "E92.4.0.8", {"start": v(-295, 1332) * mm, "mid": v(-291.46, 1333.46) * mm, "end": v(-290, 1337) * mm});
            skArc(sketch, "E92.4.0.9", {"start": v(-290, 1365) * mm, "mid": v(-291.46, 1368.54) * mm, "end": v(-295, 1370) * mm});
            skArc(sketch, "E92.4.0.10", {"start": v(-379, 1337) * mm, "mid": v(-377.54, 1333.46) * mm, "end": v(-374, 1332) * mm});
            skArc(sketch, "E92.4.0.11", {"start": v(-374, 1370) * mm, "mid": v(-377.54, 1368.54) * mm, "end": v(-379, 1365) * mm});
            skPoint(sketch, "E92.5.0.0", {"position": v(-122.25, 1370) * mm});
            skLineSegment(sketch, "E92.5.0.1", {"start": v(-206.25, 1370) * mm, "end": v(-127.25, 1370) * mm});
            skLineSegment(sketch, "E92.5.0.2", {"start": v(-206.25, 1332) * mm, "end": v(-127.25, 1332) * mm});
            skLineSegment(sketch, "E92.5.0.3", {"start": v(-122.25, 1365) * mm, "end": v(-122.25, 1337) * mm});
            skLineSegment(sketch, "E92.5.0.4", {"start": v(-211.25, 1365) * mm, "end": v(-211.25, 1337) * mm});
            skPoint(sketch, "E92.5.0.5", {"position": v(-211.25, 1370) * mm});
            skPoint(sketch, "E92.5.0.6", {"position": v(-122.25, 1332) * mm});
            skPoint(sketch, "E92.5.0.7", {"position": v(-211.25, 1332) * mm});
            skArc(sketch, "E92.5.0.8", {"start": v(-127.25, 1332) * mm, "mid": v(-123.71, 1333.46) * mm, "end": v(-122.25, 1337) * mm});
            skArc(sketch, "E92.5.0.9", {"start": v(-122.25, 1365) * mm, "mid": v(-123.71, 1368.54) * mm, "end": v(-127.25, 1370) * mm});
            skArc(sketch, "E92.5.0.10", {"start": v(-211.25, 1337) * mm, "mid": v(-209.79, 1333.46) * mm, "end": v(-206.25, 1332) * mm});
            skArc(sketch, "E92.5.0.11", {"start": v(-206.25, 1370) * mm, "mid": v(-209.79, 1368.54) * mm, "end": v(-211.25, 1365) * mm});
            skPoint(sketch, "E92.6.0.0", {"position": v(45.5, 1370) * mm});
            skLineSegment(sketch, "E92.6.0.1", {"start": v(-38.5, 1370) * mm, "end": v(40.5, 1370) * mm});
            skLineSegment(sketch, "E92.6.0.2", {"start": v(-38.5, 1332) * mm, "end": v(40.5, 1332) * mm});
            skLineSegment(sketch, "E92.6.0.3", {"start": v(45.5, 1365) * mm, "end": v(45.5, 1337) * mm});
            skLineSegment(sketch, "E92.6.0.4", {"start": v(-43.5, 1365) * mm, "end": v(-43.5, 1337) * mm});
            skPoint(sketch, "E92.6.0.5", {"position": v(-43.5, 1370) * mm});
            skPoint(sketch, "E92.6.0.6", {"position": v(45.5, 1332) * mm});
            skPoint(sketch, "E92.6.0.7", {"position": v(-43.5, 1332) * mm});
            skArc(sketch, "E92.6.0.8", {"start": v(40.5, 1332) * mm, "mid": v(44.04, 1333.46) * mm, "end": v(45.5, 1337) * mm});
            skArc(sketch, "E92.6.0.9", {"start": v(45.5, 1365) * mm, "mid": v(44.04, 1368.54) * mm, "end": v(40.5, 1370) * mm});
            skArc(sketch, "E92.6.0.10", {"start": v(-43.5, 1337) * mm, "mid": v(-42.04, 1333.46) * mm, "end": v(-38.5, 1332) * mm});
            skArc(sketch, "E92.6.0.11", {"start": v(-38.5, 1370) * mm, "mid": v(-42.04, 1368.54) * mm, "end": v(-43.5, 1365) * mm});
            skPoint(sketch, "E92.7.0.0", {"position": v(213.25, 1370) * mm});
            skLineSegment(sketch, "E92.7.0.1", {"start": v(129.25, 1370) * mm, "end": v(208.25, 1370) * mm});
            skLineSegment(sketch, "E92.7.0.2", {"start": v(129.25, 1332) * mm, "end": v(208.25, 1332) * mm});
            skLineSegment(sketch, "E92.7.0.3", {"start": v(213.25, 1365) * mm, "end": v(213.25, 1337) * mm});
            skLineSegment(sketch, "E92.7.0.4", {"start": v(124.25, 1365) * mm, "end": v(124.25, 1337) * mm});
            skPoint(sketch, "E92.7.0.5", {"position": v(124.25, 1370) * mm});
            skPoint(sketch, "E92.7.0.6", {"position": v(213.25, 1332) * mm});
            skPoint(sketch, "E92.7.0.7", {"position": v(124.25, 1332) * mm});
            skArc(sketch, "E92.7.0.8", {"start": v(208.25, 1332) * mm, "mid": v(211.79, 1333.46) * mm, "end": v(213.25, 1337) * mm});
            skArc(sketch, "E92.7.0.9", {"start": v(213.25, 1365) * mm, "mid": v(211.79, 1368.54) * mm, "end": v(208.25, 1370) * mm});
            skArc(sketch, "E92.7.0.10", {"start": v(124.25, 1337) * mm, "mid": v(125.71, 1333.46) * mm, "end": v(129.25, 1332) * mm});
            skArc(sketch, "E92.7.0.11", {"start": v(129.25, 1370) * mm, "mid": v(125.71, 1368.54) * mm, "end": v(124.25, 1365) * mm});
            skPoint(sketch, "E92.8.0.0", {"position": v(381, 1370) * mm});
            skLineSegment(sketch, "E92.8.0.1", {"start": v(297, 1370) * mm, "end": v(376, 1370) * mm});
            skLineSegment(sketch, "E92.8.0.2", {"start": v(297, 1332) * mm, "end": v(376, 1332) * mm});
            skLineSegment(sketch, "E92.8.0.3", {"start": v(381, 1365) * mm, "end": v(381, 1337) * mm});
            skLineSegment(sketch, "E92.8.0.4", {"start": v(292, 1365) * mm, "end": v(292, 1337) * mm});
            skPoint(sketch, "E92.8.0.5", {"position": v(292, 1370) * mm});
            skPoint(sketch, "E92.8.0.6", {"position": v(381, 1332) * mm});
            skPoint(sketch, "E92.8.0.7", {"position": v(292, 1332) * mm});
            skArc(sketch, "E92.8.0.8", {"start": v(376, 1332) * mm, "mid": v(379.54, 1333.46) * mm, "end": v(381, 1337) * mm});
            skArc(sketch, "E92.8.0.9", {"start": v(381, 1365) * mm, "mid": v(379.54, 1368.54) * mm, "end": v(376, 1370) * mm});
            skArc(sketch, "E92.8.0.10", {"start": v(292, 1337) * mm, "mid": v(293.46, 1333.46) * mm, "end": v(297, 1332) * mm});
            skArc(sketch, "E92.8.0.11", {"start": v(297, 1370) * mm, "mid": v(293.46, 1368.54) * mm, "end": v(292, 1365) * mm});
            skPoint(sketch, "E92.9.0.0", {"position": v(548.75, 1370) * mm});
            skLineSegment(sketch, "E92.9.0.1", {"start": v(464.75, 1370) * mm, "end": v(543.75, 1370) * mm});
            skLineSegment(sketch, "E92.9.0.2", {"start": v(464.75, 1332) * mm, "end": v(543.75, 1332) * mm});
            skLineSegment(sketch, "E92.9.0.3", {"start": v(548.75, 1365) * mm, "end": v(548.75, 1337) * mm});
            skLineSegment(sketch, "E92.9.0.4", {"start": v(459.75, 1365) * mm, "end": v(459.75, 1337) * mm});
            skPoint(sketch, "E92.9.0.5", {"position": v(459.75, 1370) * mm});
            skPoint(sketch, "E92.9.0.6", {"position": v(548.75, 1332) * mm});
            skPoint(sketch, "E92.9.0.7", {"position": v(459.75, 1332) * mm});
            skArc(sketch, "E92.9.0.8", {"start": v(543.75, 1332) * mm, "mid": v(547.29, 1333.46) * mm, "end": v(548.75, 1337) * mm});
            skArc(sketch, "E92.9.0.9", {"start": v(548.75, 1365) * mm, "mid": v(547.29, 1368.54) * mm, "end": v(543.75, 1370) * mm});
            skArc(sketch, "E92.9.0.10", {"start": v(459.75, 1337) * mm, "mid": v(461.21, 1333.46) * mm, "end": v(464.75, 1332) * mm});
            skArc(sketch, "E92.9.0.11", {"start": v(464.75, 1370) * mm, "mid": v(461.21, 1368.54) * mm, "end": v(459.75, 1365) * mm});
            skPoint(sketch, "E92.10.0.0", {"position": v(716.5, 1370) * mm});
            skLineSegment(sketch, "E92.10.0.1", {"start": v(632.5, 1370) * mm, "end": v(711.5, 1370) * mm});
            skLineSegment(sketch, "E92.10.0.2", {"start": v(632.5, 1332) * mm, "end": v(711.5, 1332) * mm});
            skLineSegment(sketch, "E92.10.0.3", {"start": v(716.5, 1365) * mm, "end": v(716.5, 1337) * mm});
            skLineSegment(sketch, "E92.10.0.4", {"start": v(627.5, 1365) * mm, "end": v(627.5, 1337) * mm});
            skPoint(sketch, "E92.10.0.5", {"position": v(627.5, 1370) * mm});
            skPoint(sketch, "E92.10.0.6", {"position": v(716.5, 1332) * mm});
            skPoint(sketch, "E92.10.0.7", {"position": v(627.5, 1332) * mm});
            skArc(sketch, "E92.10.0.8", {"start": v(711.5, 1332) * mm, "mid": v(715.04, 1333.46) * mm, "end": v(716.5, 1337) * mm});
            skArc(sketch, "E92.10.0.9", {"start": v(716.5, 1365) * mm, "mid": v(715.04, 1368.54) * mm, "end": v(711.5, 1370) * mm});
            skArc(sketch, "E92.10.0.10", {"start": v(627.5, 1337) * mm, "mid": v(628.96, 1333.46) * mm, "end": v(632.5, 1332) * mm});
            skArc(sketch, "E92.10.0.11", {"start": v(632.5, 1370) * mm, "mid": v(628.96, 1368.54) * mm, "end": v(627.5, 1365) * mm});
            skPoint(sketch, "E92.11.0.0", {"position": v(884.25, 1370) * mm});
            skLineSegment(sketch, "E92.11.0.1", {"start": v(800.25, 1370) * mm, "end": v(879.25, 1370) * mm});
            skLineSegment(sketch, "E92.11.0.2", {"start": v(800.25, 1332) * mm, "end": v(879.25, 1332) * mm});
            skLineSegment(sketch, "E92.11.0.3", {"start": v(884.25, 1365) * mm, "end": v(884.25, 1337) * mm});
            skLineSegment(sketch, "E92.11.0.4", {"start": v(795.25, 1365) * mm, "end": v(795.25, 1337) * mm});
            skPoint(sketch, "E92.11.0.5", {"position": v(795.25, 1370) * mm});
            skPoint(sketch, "E92.11.0.6", {"position": v(884.25, 1332) * mm});
            skPoint(sketch, "E92.11.0.7", {"position": v(795.25, 1332) * mm});
            skArc(sketch, "E92.11.0.8", {"start": v(879.25, 1332) * mm, "mid": v(882.79, 1333.46) * mm, "end": v(884.25, 1337) * mm});
            skArc(sketch, "E92.11.0.9", {"start": v(884.25, 1365) * mm, "mid": v(882.79, 1368.54) * mm, "end": v(879.25, 1370) * mm});
            skArc(sketch, "E92.11.0.10", {"start": v(795.25, 1337) * mm, "mid": v(796.71, 1333.46) * mm, "end": v(800.25, 1332) * mm});
            skArc(sketch, "E92.11.0.11", {"start": v(800.25, 1370) * mm, "mid": v(796.71, 1368.54) * mm, "end": v(795.25, 1365) * mm});
            skLineSegment(sketch, "E92.direction1", {"start": v(-1050, 1332) * mm, "end": v(-882.25, 1332) * mm, "construction": true});
            skPoint(sketch, "E93.0.12.0", {"position": v(1052, 1370) * mm});
            skLineSegment(sketch, "E93.1.12.0", {"start": v(968, 1370) * mm, "end": v(1047, 1370) * mm});
            skLineSegment(sketch, "E93.4.12.0", {"start": v(968, 1332) * mm, "end": v(1047, 1332) * mm});
            skLineSegment(sketch, "E93.7.12.0", {"start": v(1052, 1365) * mm, "end": v(1052, 1337) * mm});
            skLineSegment(sketch, "E93.10.12.0", {"start": v(963, 1365) * mm, "end": v(963, 1337) * mm});
            skPoint(sketch, "E93.13.12.0", {"position": v(963, 1370) * mm});
            skPoint(sketch, "E93.14.12.0", {"position": v(1052, 1332) * mm});
            skPoint(sketch, "E93.15.12.0", {"position": v(963, 1332) * mm});
            skArc(sketch, "E93.16.12.0", {"start": v(1047, 1332) * mm, "mid": v(1050.54, 1333.46) * mm, "end": v(1052, 1337) * mm});
            skArc(sketch, "E93.20.12.0", {"start": v(1052, 1365) * mm, "mid": v(1050.54, 1368.54) * mm, "end": v(1047, 1370) * mm});
            skArc(sketch, "E93.24.12.0", {"start": v(963, 1337) * mm, "mid": v(964.46, 1333.46) * mm, "end": v(968, 1332) * mm});
            skArc(sketch, "E93.28.12.0", {"start": v(968, 1370) * mm, "mid": v(964.46, 1368.54) * mm, "end": v(963, 1365) * mm});
            skSolve(sketch);
        }
        {
            var Q0;
            Q0 = qSketchRegion(id + "F10", true);
            extrude(context, id + "F11", {"entities" : qUnion([Q0]), "depth" : 650 * mm, "offsetDistance" : 25 * mm, "hasSecondDirection" : true, "secondDirectionOppositeDirection" : true, "secondDirectionDepth" : 650 * mm});
        }
        {
            var Q0;
            Q0=makeQuery(id+"F9.opExtrude","SWEPT_FACE",FACE,{"disambiguationData":[OSD([sQuery(id+"F8.wireOp",EDGE,"E86.bottom")])]});
            var Q1;
            Q1=makeQuery(id+"F9.opExtrude","SWEPT_FACE",FACE,{"disambiguationData":[OSD([sQuery(id+"F8.wireOp",EDGE,"E86.top")])]});
            var Q2;
            Q2=makeQuery(id+"F9.opExtrude","CAP_FACE",FACE,{"disambiguationData":[OSD([sQuery(id+"F8.wireOp",EDGE,"E86.bottom"),sQuery(id+"F8.wireOp",EDGE,"E86.top"),sQuery(id+"F8.wireOp",EDGE,"E86.left"),sQuery(id+"F8.wireOp",EDGE,"E86.right")])],"isStart":false});
            var Q3;
            Q3=makeQuery(id+"F9.opExtrude","CAP_FACE",FACE,{"disambiguationData":[OSD([sQuery(id+"F8.wireOp",EDGE,"E86.bottom"),sQuery(id+"F8.wireOp",EDGE,"E86.top"),sQuery(id+"F8.wireOp",EDGE,"E86.left"),sQuery(id+"F8.wireOp",EDGE,"E86.right")])],"isStart":true});
            fillet(context, id + "F12", {"entities" : qUnion([Q0, Q1, Q2, Q3]), "radius" : 5 * mm, "tangentPropagation" : true, "allowEdgeOverflow" : false});
        }
        {
            var Q0;
            Q0=makeQuery(id+"F7.opExtrude","CAP_FACE",FACE,{"disambiguationData":[OSD([sQuery(id+"F6.wireOp",EDGE,"E80.bottom"),sQuery(id+"F6.wireOp",EDGE,"E80.top"),sQuery(id+"F6.wireOp",EDGE,"E80.left"),sQuery(id+"F6.wireOp",EDGE,"E80.right"),sQuery(id+"F6.wireOp",EDGE,"E81.filletArc"),sQuery(id+"F6.wireOp",EDGE,"E82.filletArc"),sQuery(id+"F6.wireOp",EDGE,"E83.filletArc"),sQuery(id+"F6.wireOp",EDGE,"E84.filletArc")])],"isStart":false});
            var Q1;
            Q1=makeQuery(id+"F7.opExtrude","CAP_FACE",FACE,{"disambiguationData":[OSD([sQuery(id+"F6.wireOp",EDGE,"E80.bottom"),sQuery(id+"F6.wireOp",EDGE,"E80.top"),sQuery(id+"F6.wireOp",EDGE,"E80.left"),sQuery(id+"F6.wireOp",EDGE,"E80.right"),sQuery(id+"F6.wireOp",EDGE,"E81.filletArc"),sQuery(id+"F6.wireOp",EDGE,"E82.filletArc"),sQuery(id+"F6.wireOp",EDGE,"E83.filletArc"),sQuery(id+"F6.wireOp",EDGE,"E84.filletArc")])],"isStart":true});
            fillet(context, id + "F13", {"entities" : qUnion([Q0, Q1]), "radius" : 25 * mm, "tangentPropagation" : true, "allowEdgeOverflow" : false});
        }
        {
            var Q0;
            Q0=makeQuery(id+"F9.opExtrude","CAP_FACE",FACE,{"disambiguationData":[OSD([sQuery(id+"F8.wireOp",EDGE,"E85.bottom"),sQuery(id+"F8.wireOp",EDGE,"E85.top"),sQuery(id+"F8.wireOp",EDGE,"E85.left"),sQuery(id+"F8.wireOp",EDGE,"E85.right")])],"isStart":true});
            var Q1;
            Q1=makeQuery(id+"F9.opExtrude","CAP_FACE",FACE,{"disambiguationData":[OSD([sQuery(id+"F8.wireOp",EDGE,"E85.bottom"),sQuery(id+"F8.wireOp",EDGE,"E85.top"),sQuery(id+"F8.wireOp",EDGE,"E85.left"),sQuery(id+"F8.wireOp",EDGE,"E85.right")])],"isStart":false});
            var Q2;
            Q2=makeQuery(id+"F9.opExtrude","SWEPT_FACE",FACE,{"disambiguationData":[OSD([sQuery(id+"F8.wireOp",EDGE,"E85.right")])]});
            var Q3;
            Q3=makeQuery(id+"F9.opExtrude","SWEPT_FACE",FACE,{"disambiguationData":[OSD([sQuery(id+"F8.wireOp",EDGE,"E85.left")])]});
            fillet(context, id + "F14", {"entities" : qUnion([Q0, Q1, Q2, Q3]), "radius" : 5 * mm, "tangentPropagation" : true, "allowEdgeOverflow" : false});
        }
        {
            var Q0;
            Q0=makeQuery(id+"F1.opExtrude","CAP_FACE",FACE,{"disambiguationData":[OSD([sQuery(id+"F0.wireOp",EDGE,"E3.bottom"),sQuery(id+"F0.wireOp",EDGE,"E3.top"),sQuery(id+"F0.wireOp",EDGE,"E3.left"),sQuery(id+"F0.wireOp",EDGE,"E3.right"),sQuery(id+"F0.wireOp",EDGE,"E16.filletArc"),sQuery(id+"F0.wireOp",EDGE,"E17.filletArc"),sQuery(id+"F0.wireOp",EDGE,"E18.filletArc"),sQuery(id+"F0.wireOp",EDGE,"E19.filletArc")])],"isStart":false});
            var Q1;
            Q1=makeQuery(id+"F1.opExtrude","CAP_FACE",FACE,{"disambiguationData":[OSD([sQuery(id+"F0.wireOp",EDGE,"E0.bottom"),sQuery(id+"F0.wireOp",EDGE,"E0.top"),sQuery(id+"F0.wireOp",EDGE,"E0.left"),sQuery(id+"F0.wireOp",EDGE,"E0.right"),sQuery(id+"F0.wireOp",EDGE,"E12.filletArc"),sQuery(id+"F0.wireOp",EDGE,"E13.filletArc"),sQuery(id+"F0.wireOp",EDGE,"E14.filletArc"),sQuery(id+"F0.wireOp",EDGE,"E15.filletArc")])],"isStart":false});
            var Q2;
            Q2=makeQuery(id+"F3.opExtrude","CAP_FACE",FACE,{"disambiguationData":[OSD([sQuery(id+"F2.wireOp",EDGE,"E20.bottom"),sQuery(id+"F2.wireOp",EDGE,"E20.top"),sQuery(id+"F2.wireOp",EDGE,"E20.left"),sQuery(id+"F2.wireOp",EDGE,"E20.right"),sQuery(id+"F2.wireOp",EDGE,"E29.filletArc"),sQuery(id+"F2.wireOp",EDGE,"E30.filletArc"),sQuery(id+"F2.wireOp",EDGE,"E31.filletArc"),sQuery(id+"F2.wireOp",EDGE,"E32.filletArc")])],"isStart":false});
            var Q3;
            Q3=makeQuery(id+"F3.opExtrude","CAP_FACE",FACE,{"disambiguationData":[OSD([sQuery(id+"F2.wireOp",EDGE,"E23.bottom"),sQuery(id+"F2.wireOp",EDGE,"E23.top"),sQuery(id+"F2.wireOp",EDGE,"E23.left"),sQuery(id+"F2.wireOp",EDGE,"E23.right"),sQuery(id+"F2.wireOp",EDGE,"E25.filletArc"),sQuery(id+"F2.wireOp",EDGE,"E26.filletArc"),sQuery(id+"F2.wireOp",EDGE,"E27.filletArc"),sQuery(id+"F2.wireOp",EDGE,"E28.filletArc")])],"isStart":false});
            var Q4;
            Q4=makeQuery(id+"F3.opExtrude","CAP_FACE",FACE,{"disambiguationData":[OSD([sQuery(id+"F2.wireOp",EDGE,"E21.bottom"),sQuery(id+"F2.wireOp",EDGE,"E21.top"),sQuery(id+"F2.wireOp",EDGE,"E21.left"),sQuery(id+"F2.wireOp",EDGE,"E21.right"),sQuery(id+"F2.wireOp",EDGE,"E37.filletArc"),sQuery(id+"F2.wireOp",EDGE,"E38.filletArc"),sQuery(id+"F2.wireOp",EDGE,"E39.filletArc"),sQuery(id+"F2.wireOp",EDGE,"E40.filletArc")])],"isStart":false});
            var Q5;
            Q5=makeQuery(id+"F3.opExtrude","CAP_FACE",FACE,{"disambiguationData":[OSD([sQuery(id+"F2.wireOp",EDGE,"E24.bottom"),sQuery(id+"F2.wireOp",EDGE,"E24.top"),sQuery(id+"F2.wireOp",EDGE,"E24.left"),sQuery(id+"F2.wireOp",EDGE,"E24.right"),sQuery(id+"F2.wireOp",EDGE,"E33.filletArc"),sQuery(id+"F2.wireOp",EDGE,"E34.filletArc"),sQuery(id+"F2.wireOp",EDGE,"E35.filletArc"),sQuery(id+"F2.wireOp",EDGE,"E36.filletArc")])],"isStart":false});
            var Q6;
            Q6=makeQuery(id+"F3.opExtrude","CAP_FACE",FACE,{"disambiguationData":[OSD([sQuery(id+"F2.wireOp",EDGE,"E22.bottom"),sQuery(id+"F2.wireOp",EDGE,"E22.top"),sQuery(id+"F2.wireOp",EDGE,"E22.left"),sQuery(id+"F2.wireOp",EDGE,"E22.right"),sQuery(id+"F2.wireOp",EDGE,"E41.filletArc"),sQuery(id+"F2.wireOp",EDGE,"E42.filletArc"),sQuery(id+"F2.wireOp",EDGE,"E43.filletArc"),sQuery(id+"F2.wireOp",EDGE,"E44.filletArc")])],"isStart":false});
            var Q7;
            Q7=makeQuery(id+"F1.opExtrude","CAP_FACE",FACE,{"disambiguationData":[OSD([sQuery(id+"F0.wireOp",EDGE,"E2.bottom"),sQuery(id+"F0.wireOp",EDGE,"E2.top"),sQuery(id+"F0.wireOp",EDGE,"E2.left"),sQuery(id+"F0.wireOp",EDGE,"E2.right"),sQuery(id+"F0.wireOp",EDGE,"E8.filletArc"),sQuery(id+"F0.wireOp",EDGE,"E9.filletArc"),sQuery(id+"F0.wireOp",EDGE,"E10.filletArc"),sQuery(id+"F0.wireOp",EDGE,"E11.filletArc")])],"isStart":false});
            var Q8;
            Q8=makeQuery(id+"F1.opExtrude","CAP_FACE",FACE,{"disambiguationData":[OSD([sQuery(id+"F0.wireOp",EDGE,"E1.bottom"),sQuery(id+"F0.wireOp",EDGE,"E1.top"),sQuery(id+"F0.wireOp",EDGE,"E1.left"),sQuery(id+"F0.wireOp",EDGE,"E1.right"),sQuery(id+"F0.wireOp",EDGE,"E4.filletArc"),sQuery(id+"F0.wireOp",EDGE,"E5.filletArc"),sQuery(id+"F0.wireOp",EDGE,"E6.filletArc"),sQuery(id+"F0.wireOp",EDGE,"E7.filletArc")])],"isStart":false});
            var Q9;
            Q9=makeQuery(id+"F3.opExtrude","CAP_FACE",FACE,{"disambiguationData":[OSD([sQuery(id+"F2.wireOp",EDGE,"E24.bottom"),sQuery(id+"F2.wireOp",EDGE,"E24.top"),sQuery(id+"F2.wireOp",EDGE,"E24.left"),sQuery(id+"F2.wireOp",EDGE,"E24.right"),sQuery(id+"F2.wireOp",EDGE,"E33.filletArc"),sQuery(id+"F2.wireOp",EDGE,"E34.filletArc"),sQuery(id+"F2.wireOp",EDGE,"E35.filletArc"),sQuery(id+"F2.wireOp",EDGE,"E36.filletArc")])],"isStart":true});
            var Q10;
            Q10=makeQuery(id+"F3.opExtrude","CAP_FACE",FACE,{"disambiguationData":[OSD([sQuery(id+"F2.wireOp",EDGE,"E21.bottom"),sQuery(id+"F2.wireOp",EDGE,"E21.top"),sQuery(id+"F2.wireOp",EDGE,"E21.left"),sQuery(id+"F2.wireOp",EDGE,"E21.right"),sQuery(id+"F2.wireOp",EDGE,"E37.filletArc"),sQuery(id+"F2.wireOp",EDGE,"E38.filletArc"),sQuery(id+"F2.wireOp",EDGE,"E39.filletArc"),sQuery(id+"F2.wireOp",EDGE,"E40.filletArc")])],"isStart":true});
            var Q11;
            Q11=makeQuery(id+"F3.opExtrude","CAP_FACE",FACE,{"disambiguationData":[OSD([sQuery(id+"F2.wireOp",EDGE,"E23.bottom"),sQuery(id+"F2.wireOp",EDGE,"E23.top"),sQuery(id+"F2.wireOp",EDGE,"E23.left"),sQuery(id+"F2.wireOp",EDGE,"E23.right"),sQuery(id+"F2.wireOp",EDGE,"E25.filletArc"),sQuery(id+"F2.wireOp",EDGE,"E26.filletArc"),sQuery(id+"F2.wireOp",EDGE,"E27.filletArc"),sQuery(id+"F2.wireOp",EDGE,"E28.filletArc")])],"isStart":true});
            var Q12;
            Q12=makeQuery(id+"F3.opExtrude","CAP_FACE",FACE,{"disambiguationData":[OSD([sQuery(id+"F2.wireOp",EDGE,"E20.bottom"),sQuery(id+"F2.wireOp",EDGE,"E20.top"),sQuery(id+"F2.wireOp",EDGE,"E20.left"),sQuery(id+"F2.wireOp",EDGE,"E20.right"),sQuery(id+"F2.wireOp",EDGE,"E29.filletArc"),sQuery(id+"F2.wireOp",EDGE,"E30.filletArc"),sQuery(id+"F2.wireOp",EDGE,"E31.filletArc"),sQuery(id+"F2.wireOp",EDGE,"E32.filletArc")])],"isStart":true});
            var Q13;
            Q13=makeQuery(id+"F3.opExtrude","CAP_FACE",FACE,{"disambiguationData":[OSD([sQuery(id+"F2.wireOp",EDGE,"E22.bottom"),sQuery(id+"F2.wireOp",EDGE,"E22.top"),sQuery(id+"F2.wireOp",EDGE,"E22.left"),sQuery(id+"F2.wireOp",EDGE,"E22.right"),sQuery(id+"F2.wireOp",EDGE,"E41.filletArc"),sQuery(id+"F2.wireOp",EDGE,"E42.filletArc"),sQuery(id+"F2.wireOp",EDGE,"E43.filletArc"),sQuery(id+"F2.wireOp",EDGE,"E44.filletArc")])],"isStart":true});
            var Q14;
            Q14=makeQuery(id+"F3.opExtrude","CAP_FACE",FACE,{"disambiguationData":[OSD([sQuery(id+"F2.wireOp",EDGE,"E45.bottom"),sQuery(id+"F2.wireOp",EDGE,"E45.top"),sQuery(id+"F2.wireOp",EDGE,"E45.left"),sQuery(id+"F2.wireOp",EDGE,"E45.right"),sQuery(id+"F2.wireOp",EDGE,"E46.filletArc"),sQuery(id+"F2.wireOp",EDGE,"E47.filletArc"),sQuery(id+"F2.wireOp",EDGE,"E48.filletArc"),sQuery(id+"F2.wireOp",EDGE,"E49.filletArc")])],"isStart":false});
            var Q15;
            Q15=makeQuery(id+"F3.opExtrude","CAP_FACE",FACE,{"disambiguationData":[OSD([sQuery(id+"F2.wireOp",EDGE,"I1DJuX3a-8bTd-Pnxl-fgE0-B51OfbXifG51.bottom"),sQuery(id+"F2.wireOp",EDGE,"I1DJuX3a-8bTd-Pnxl-fgE0-B51OfbXifG51.top"),sQuery(id+"F2.wireOp",EDGE,"I1DJuX3a-8bTd-Pnxl-fgE0-B51OfbXifG51.left"),sQuery(id+"F2.wireOp",EDGE,"I1DJuX3a-8bTd-Pnxl-fgE0-B51OfbXifG51.right"),sQuery(id+"F2.wireOp",EDGE,"35353552-e06c-4ffc-b7e9-5466d4d0743b.filletArc"),sQuery(id+"F2.wireOp",EDGE,"f10e2773-51a1-486b-bbe5-ce32a89cabf7.filletArc"),sQuery(id+"F2.wireOp",EDGE,"0c2413b2-11e2-4840-b278-42feac7cd9b2.filletArc"),sQuery(id+"F2.wireOp",EDGE,"561077ef-e18f-4397-af2a-b468be595d31.filletArc")])],"isStart":false});
            var Q16;
            Q16=makeQuery(id+"F3.opExtrude","CAP_FACE",FACE,{"disambiguationData":[OSD([sQuery(id+"F2.wireOp",EDGE,"I1DJuX3a-8bTd-Pnxl-fgE0-B51OfbXifG51.bottom"),sQuery(id+"F2.wireOp",EDGE,"I1DJuX3a-8bTd-Pnxl-fgE0-B51OfbXifG51.top"),sQuery(id+"F2.wireOp",EDGE,"I1DJuX3a-8bTd-Pnxl-fgE0-B51OfbXifG51.left"),sQuery(id+"F2.wireOp",EDGE,"I1DJuX3a-8bTd-Pnxl-fgE0-B51OfbXifG51.right"),sQuery(id+"F2.wireOp",EDGE,"35353552-e06c-4ffc-b7e9-5466d4d0743b.filletArc"),sQuery(id+"F2.wireOp",EDGE,"f10e2773-51a1-486b-bbe5-ce32a89cabf7.filletArc"),sQuery(id+"F2.wireOp",EDGE,"0c2413b2-11e2-4840-b278-42feac7cd9b2.filletArc"),sQuery(id+"F2.wireOp",EDGE,"561077ef-e18f-4397-af2a-b468be595d31.filletArc")])],"isStart":true});
            var Q17;
            Q17=makeQuery(id+"F3.opExtrude","CAP_FACE",FACE,{"disambiguationData":[OSD([sQuery(id+"F2.wireOp",EDGE,"E45.bottom"),sQuery(id+"F2.wireOp",EDGE,"E45.top"),sQuery(id+"F2.wireOp",EDGE,"E45.left"),sQuery(id+"F2.wireOp",EDGE,"E45.right"),sQuery(id+"F2.wireOp",EDGE,"E46.filletArc"),sQuery(id+"F2.wireOp",EDGE,"E47.filletArc"),sQuery(id+"F2.wireOp",EDGE,"E48.filletArc"),sQuery(id+"F2.wireOp",EDGE,"E49.filletArc")])],"isStart":true});
            fillet(context, id + "F15", {"entities" : qUnion([Q0, Q1, Q2, Q3, Q4, Q5, Q6, Q7, Q8, Q9, Q10, Q11, Q12, Q13, Q14, Q15, Q16, Q17]), "radius" : 5 * mm, "tangentPropagation" : true, "allowEdgeOverflow" : false});
        }
    });
